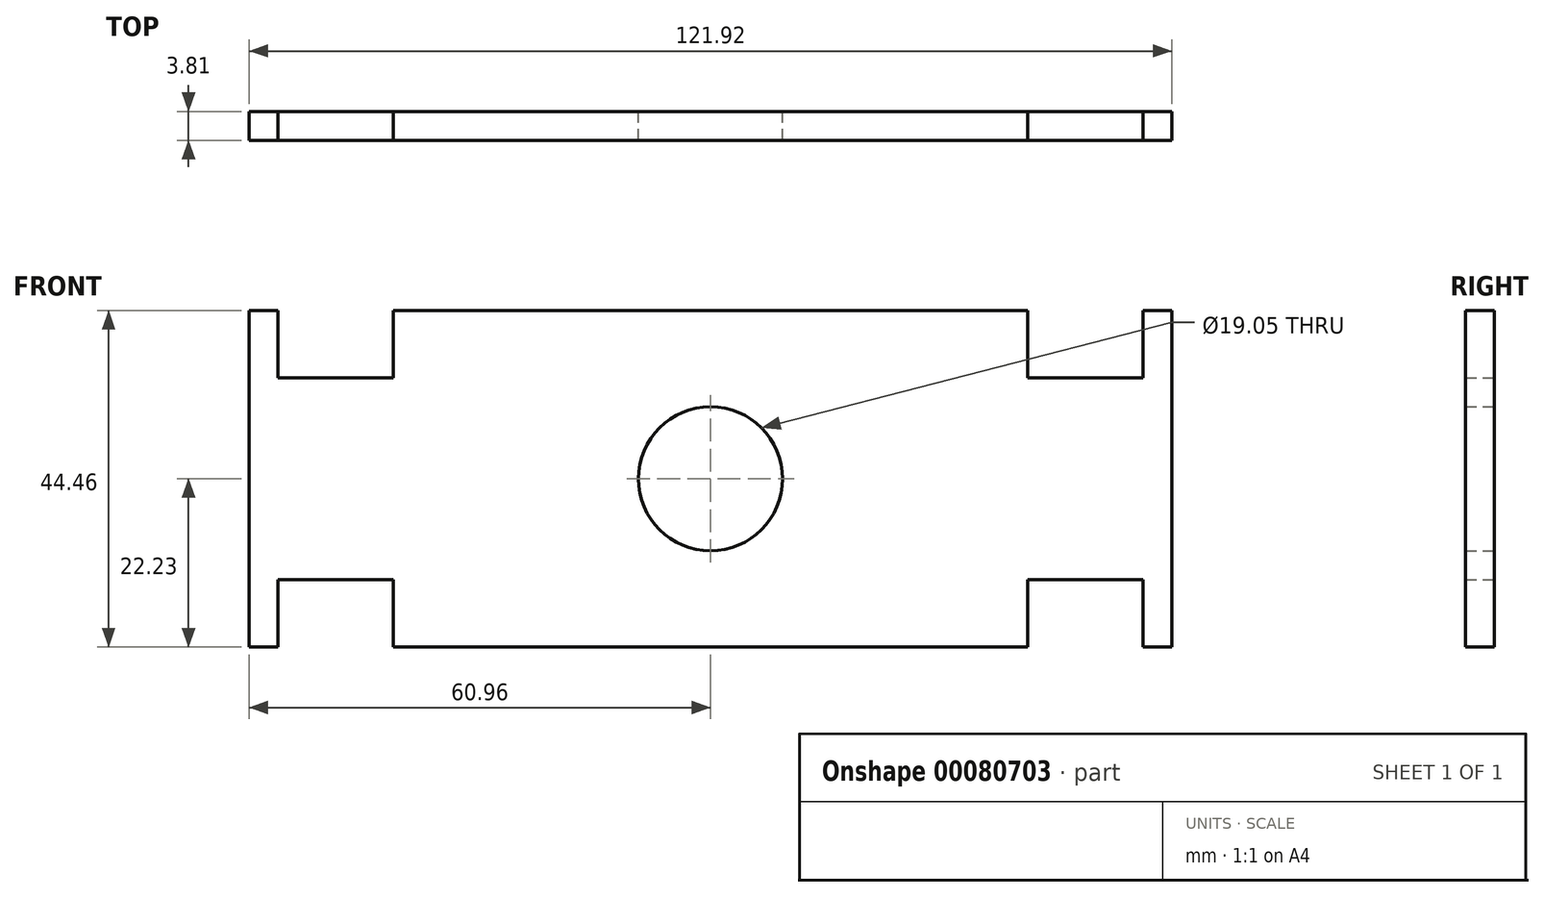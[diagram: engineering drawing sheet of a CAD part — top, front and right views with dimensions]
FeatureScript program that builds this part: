
annotation { "Feature Type Name" : "Feature", "Feature Type Description" : "" }
export const myFeature = defineFeature(function(context is Context, id is Id, definition is map)
    precondition{}
    {
        {
            var Q0;
            Q0=qCreatedBy(makeId("Front.planeOp"),FACE);
            var sketch = newSketch(context, id + "F0", { "sketchPlane" : qUnion([Q0])});
            skLineSegment(sketch, "E0.bottom", {"start": v(60.96, -22.23) * mm, "end": v(-60.96, -22.23) * mm});
            skLineSegment(sketch, "E0.top", {"start": v(60.96, 22.23) * mm, "end": v(-60.96, 22.23) * mm});
            skLineSegment(sketch, "E0.left", {"start": v(60.96, -22.23) * mm, "end": v(60.96, 22.23) * mm});
            skLineSegment(sketch, "E0.right", {"start": v(-60.96, -22.23) * mm, "end": v(-60.96, 22.23) * mm});
            skPoint(sketch, "E0.middle", {"position": v(0, 0) * mm});
            skLineSegment(sketch, "E1.bottom", {"start": v(-57.15, 22.23) * mm, "end": v(-41.9, 22.23) * mm});
            skLineSegment(sketch, "E1.top", {"start": v(-57.15, 13.34) * mm, "end": v(-41.9, 13.34) * mm});
            skLineSegment(sketch, "E1.left", {"start": v(-57.15, 22.23) * mm, "end": v(-57.15, 13.34) * mm});
            skLineSegment(sketch, "E1.right", {"start": v(-41.91, 22.23) * mm, "end": v(-41.91, 13.34) * mm});
            skLineSegment(sketch, "E2.MirrorCS", {"start": v(41.91, 22.23) * mm, "end": v(41.91, 13.34) * mm});
            skLineSegment(sketch, "E3.MirrorCS", {"start": v(-60.96, -22.23) * mm, "end": v(60.96, -22.22) * mm});
            skLineSegment(sketch, "E4.MirrorCS", {"start": v(-60.96, 22.22) * mm, "end": v(60.96, 22.23) * mm});
            skLineSegment(sketch, "E5.MirrorCS", {"start": v(57.15, 22.23) * mm, "end": v(41.9, 22.23) * mm});
            skLineSegment(sketch, "E6.MirrorCS", {"start": v(57.15, 13.34) * mm, "end": v(41.9, 13.34) * mm});
            skLineSegment(sketch, "E7.MirrorCS", {"start": v(57.15, 22.23) * mm, "end": v(57.15, 13.34) * mm});
            skLineSegment(sketch, "E8.MirrorCS", {"start": v(60.96, 22.23) * mm, "end": v(-60.96, 22.22) * mm});
            skLineSegment(sketch, "E9.MirrorCS", {"start": v(60.96, 22.23) * mm, "end": v(60.96, -22.23) * mm});
            skLineSegment(sketch, "E10.MirrorCS", {"start": v(-60.96, 22.23) * mm, "end": v(-60.96, -22.23) * mm});
            skLineSegment(sketch, "E11.MirrorCS", {"start": v(-57.15, -22.23) * mm, "end": v(-57.15, -13.34) * mm});
            skLineSegment(sketch, "E12.MirrorCS", {"start": v(-57.15, -13.34) * mm, "end": v(-41.9, -13.34) * mm});
            skLineSegment(sketch, "E13.MirrorCS", {"start": v(-57.15, -22.23) * mm, "end": v(-41.9, -22.23) * mm});
            skLineSegment(sketch, "E14.MirrorCS", {"start": v(-41.91, -22.23) * mm, "end": v(-41.91, -13.34) * mm});
            skLineSegment(sketch, "E15.MirrorCS", {"start": v(41.91, -22.23) * mm, "end": v(41.91, -13.34) * mm});
            skLineSegment(sketch, "E16.MirrorCS", {"start": v(-60.96, 22.23) * mm, "end": v(60.96, 22.23) * mm});
            skLineSegment(sketch, "E17.MirrorCS", {"start": v(-60.96, -22.23) * mm, "end": v(60.96, -22.23) * mm});
            skLineSegment(sketch, "E18.MirrorCS", {"start": v(57.15, -22.23) * mm, "end": v(41.9, -22.23) * mm});
            skLineSegment(sketch, "E19.MirrorCS", {"start": v(57.15, -13.34) * mm, "end": v(41.9, -13.34) * mm});
            skLineSegment(sketch, "E20.MirrorCS", {"start": v(57.15, -22.23) * mm, "end": v(57.15, -13.34) * mm});
            skCircle(sketch, "E21", {"center": v(0, 0) * mm, "radius": 9.53 * mm});
            skSolve(sketch);
        }
        {
            var Q0;
            Q0=makeQuery(id+"F0.imprint","IMPRINT",FACE,{"disambiguationData":[TD([[makeQuery(id+"F0.imprint","IMPRINT",EDGE,{"derivedFrom":sQuery(id+"F0.wireOp",EDGE,"E1.top")}),-1.0]])]});
            extrude(context, id + "F1", {"entities" : qUnion([Q0]), "depth" : 3.8 * mm});
        }
    });
